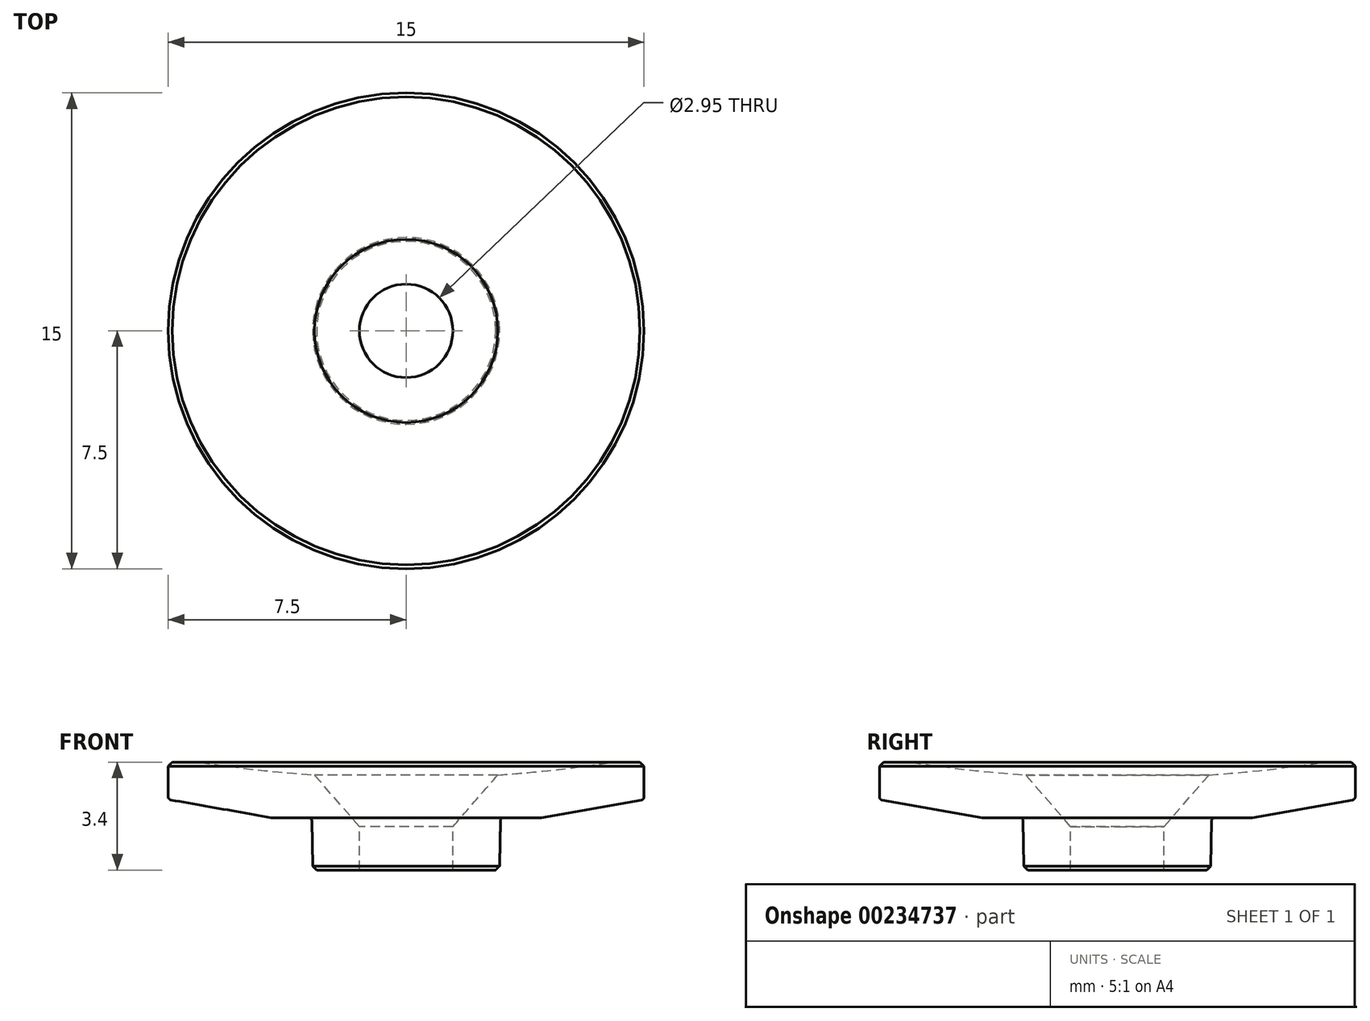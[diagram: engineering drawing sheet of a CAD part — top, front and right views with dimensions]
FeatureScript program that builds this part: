
annotation { "Feature Type Name" : "Feature", "Feature Type Description" : "" }
export const myFeature = defineFeature(function(context is Context, id is Id, definition is map)
    precondition{}
    {
        {
            var Q0;
            Q0=qCreatedBy(makeId("Front.planeOp"),FACE);
            var sketch = newSketch(context, id + "F0", { "sketchPlane" : qUnion([Q0])});
            skLineSegment(sketch, "E0", {"start": v(0, 0) * mm, "end": v(2.95, 0) * mm});
            skLineSegment(sketch, "E1", {"start": v(2.95, 0) * mm, "end": v(2.97, 1.65) * mm});
            skLineSegment(sketch, "E2", {"start": v(2.97, 1.65) * mm, "end": v(4.24, 1.65) * mm});
            skLineSegment(sketch, "E3", {"start": v(4.24, 1.65) * mm, "end": v(7.5, 2.22) * mm});
            skLineSegment(sketch, "E4", {"start": v(7.5, 2.22) * mm, "end": v(7.5, 3.4) * mm});
            skLineSegment(sketch, "E5", {"start": v(7.5, 3.4) * mm, "end": v(6.5, 3.4) * mm});
            skLineSegment(sketch, "E6", {"start": v(0, 2.9) * mm, "end": v(0, 0) * mm});
            skArc(sketch, "E7", {"start": v(0, 2.9) * mm, "mid": v(3.26, 3.03) * mm, "end": v(6.5, 3.4) * mm});
            skPoint(sketch, "E8.orphan", {"position": v(0, 3.4) * mm});
            skLineSegment(sketch, "E9", {"start": v(0, 0) * mm, "end": v(0, -2.37) * mm, "construction": true});
            skSolve(sketch);
        }
        {
            var Q0;
            Q0=qSketchRegion(id+"F0",true);
            var Q1;
            Q1=sQuery(id+"F0.wireOp",EDGE,"E6");
            revolve(context, id + "F1", {"entities" : qUnion([Q0]), "axis" : qUnion([Q1]), "revolveType" : RevolveType.FULL});
        }
        {
            var Q0;
            Q0=makeQuery(id+"F1.opRevolve","SWEPT_EDGE",EDGE,{"disambiguationData":[OSD([sQuery(id+"F0.wireOp",EDGE,"E0"),sQuery(id+"F0.wireOp",EDGE,"E1")])]});
            var Q1;
            Q1=makeQuery(id+"F1.opRevolve","SWEPT_EDGE",EDGE,{"disambiguationData":[OSD([sQuery(id+"F0.wireOp",EDGE,"E4"),sQuery(id+"F0.wireOp",EDGE,"E5")])]});
            chamfer(context, id + "F2", {"entities" : qUnion([Q0, Q1]), "width" : 0.13 * mm, "tangentPropagation" : true});
        }
        {
            var Q0;
            Q0=makeQuery(id+"F1.opRevolve","SWEPT_EDGE",EDGE,{"disambiguationData":[OSD([sQuery(id+"F0.wireOp",EDGE,"KmEllf09-JBKP-2wvp-Ln3d-dT31Av5gxA5O"),sQuery(id+"F0.wireOp",EDGE,"SqjkA4CO-rQVQ-ybkh-YT7C-LuhsKEooFiCv")])]});
            var Q1;
            Q1=makeQuery(id+"F1.opRevolve","SWEPT_EDGE",EDGE,{"disambiguationData":[OSD([sQuery(id+"F0.wireOp",EDGE,"E3"),sQuery(id+"F0.wireOp",EDGE,"KmEllf09-JBKP-2wvp-Ln3d-dT31Av5gxA5O")])]});
            var Q2;
            Q2=makeQuery(id+"F1.opRevolve","SWEPT_EDGE",EDGE,{"disambiguationData":[OSD([sQuery(id+"F0.wireOp",EDGE,"E2"),sQuery(id+"F0.wireOp",EDGE,"E3")])]});
            var Q3;
            Q3=makeQuery(id+"F1.opRevolve","SWEPT_EDGE",EDGE,{"disambiguationData":[OSD([sQuery(id+"F0.wireOp",EDGE,"E5"),sQuery(id+"F0.wireOp",EDGE,"E7")])]});
            var Q4;
            Q4=makeQuery(id+"F1.opRevolve","SWEPT_EDGE",EDGE,{"disambiguationData":[OSD([sQuery(id+"F0.wireOp",EDGE,"E1"),sQuery(id+"F0.wireOp",EDGE,"E2")])]});
            fillet(context, id + "F3", {"entities" : qUnion([Q0, Q1, Q2, Q3, Q4]), "radius" : .1 * mm, "tangentPropagation" : true, "allowEdgeOverflow" : false});
        }
        {
            var Q0;
            Q0=makeQuery(id+"F1.opRevolve","SWEPT_FACE",FACE,{"disambiguationData":[OSD([sQuery(id+"F0.wireOp",EDGE,"E5")])]});
            var sketch = newSketch(context, id + "F4", { "sketchPlane" : qUnion([Q0])});
            skPoint(sketch, "E10.0", {"position": v(0, 0) * mm});
            skSolve(sketch);
        }
        {
            var Q0;
            Q0=sQuery(id+"F4.wireOp",VERTEX,"E10.0");
            var Q1;
            Q1=makeQuery(id+"F1.opRevolve","SWEPT_BODY",BODY,{"disambiguationData":[OSD([sQuery(id+"F0.wireOp",EDGE,"E0"),sQuery(id+"F0.wireOp",EDGE,"E1"),sQuery(id+"F0.wireOp",EDGE,"E2"),sQuery(id+"F0.wireOp",EDGE,"E3"),sQuery(id+"F0.wireOp",EDGE,"E4"),sQuery(id+"F0.wireOp",EDGE,"E5"),sQuery(id+"F0.wireOp",EDGE,"E6"),sQuery(id+"F0.wireOp",EDGE,"E7")])]});
            hole(context, id + "F5", {"style" : HoleStyle.C_SINK, "endStyle" : HoleEndStyle.BLIND, "standardTappedOrClearance" : lookupTablePath({ "standard" : "ANSI", "fit" : "Close", "size" : "#4", "type" : "Clearance" }), "standardBlindInLast" : lookupTablePath({ "fit" : "Close", "standard" : "ANSI", "size" : "#4", "type" : "Clearance" }), "holeDiameter" : 2.95 * mm, "cSinkDiameter" : 6.48 * mm, "cSinkAngle" : 82 * degree, "holeDepth" : 12.7 * mm, "startFromSketch" : true, "locations" : qUnion([Q0]), "scope" : qUnion([Q1])});
        }
    });
